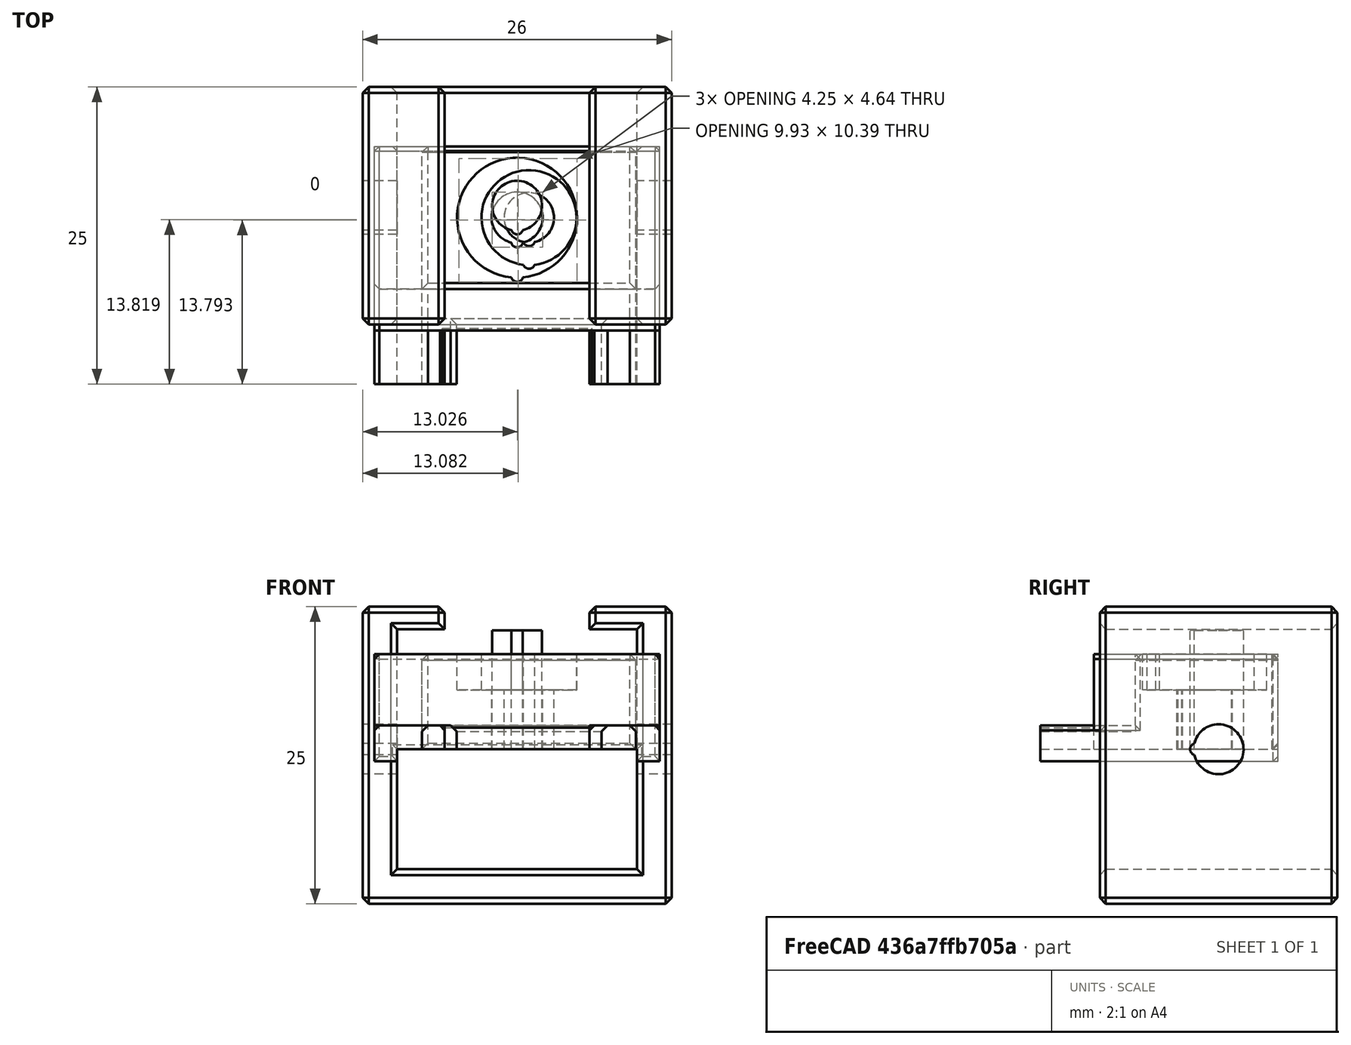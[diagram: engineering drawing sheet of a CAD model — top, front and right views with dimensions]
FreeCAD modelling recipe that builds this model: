
FCSTD DOCUMENT  (FreeCAD 0.18R14555 (Git shallow))
Label: 2020-rail-mount
License: All rights reserved
LicenseURL: http://en.wikipedia.org/wiki/All_rights_reserved
objects: Part::Box×9, Part::Cut×7, Part::Cylinder×6, Part::Feature×6, Part::MultiFuse×6, Part::Chamfer×5
note: 39 computed .brp shape members not serialized (recipe doc carries the construction recipe); baked Part::Feature solids carry a one-line shape summary decoded from their .brp

FEATURE [Part::Box] Box  label="Cube"
  AttacherType = Attacher::AttachEngine3D
  Height = 8
  Length = 24
  Placement = pos=(-12,3,0) rot=(0,0,1;0rad)
  Width = 12
FEATURE [Part::Box] Box001  label="ref"
  AttacherType = Attacher::AttachEngine3D
  Height = 2
  Length = 12.2
  Placement = pos=(-6.1,-5,0) rot=(0,0,1;0rad)
  Width = 4.5
FEATURE [Part::Cylinder] Cylinder
  Angle = 360
  AttacherType = Attacher::AttachEngine3D
  Height = 8
  Placement = pos=(0,7,0) rot=(0,0,1;0rad)
  Radius = 0.5
FEATURE [Part::Feature] Cut001001  label="Cut002"
  shape: bbox 18 x 20 x 8 mm, 17 faces (baked)
FEATURE [Part::Chamfer] Chamfer  label="head-tail"
  Base = -> Cut001001
  Edges = 12 edges r=0.5: [Edge1,Edge3,Edge5,Edge6,Edge7,Edge13,Edge15,Edge16,Edge17,Edge33,Edge34,Edge35]
FEATURE [Part::Box] Box003  label="Cube003"
  AttacherType = Attacher::AttachEngine3D
  Height = 20.2
  Length = 20.2
  Placement = pos=(-10.1,0,-10.1) rot=(0,0,1;0rad)
  Width = 20
FEATURE [Part::Box] Box004  label="Cube004"
  AttacherType = Attacher::AttachEngine3D
  Height = 25
  Length = 26
  Placement = pos=(-13,0,-13) rot=(0,0,1;0rad)
  Width = 20
FEATURE [Part::Box] Box005  label="Cube005"
  AttacherType = Attacher::AttachEngine3D
  Height = 13
  Length = 12.2
  Placement = pos=(-6.1,0,0) rot=(0,0,1;0rad)
  Width = 20
FEATURE [Part::MultiFuse] Fusion002
  Shapes = -> [Box003,Box005]
FEATURE [Part::Cylinder] Cylinder004
  Angle = 360
  AttacherType = Attacher::AttachEngine3D
  Height = 10
  Placement = pos=(0,10,0) rot=(0,0,1;0rad)
  Radius = 2.1
FEATURE [Part::Cylinder] Cylinder005
  Angle = 360
  AttacherType = Attacher::AttachEngine3D
  Height = 10
  Placement = pos=(0,8.1,0) rot=(0,0,1;0rad)
  Radius = 0.5
FEATURE [Part::MultiFuse] Fusion003
  Shapes = -> [Cylinder005,Cylinder004]
FEATURE [Part::Feature] Fusion003001  label="Fusion004"
  Placement = pos=(-6.7,0,-1e-15) rot=(0,-1,0;1.5708rad)
  shape: bbox 10 x 4.5 x 4.2 mm, 9 faces (baked)
FEATURE [Part::Feature] Fusion003002  label="Fusion005"
  Placement = pos=(14.7,0,-5.8e-15) rot=(0,-1,0;1.5708rad)
  shape: bbox 10 x 4.5 x 4.2 mm, 9 faces (baked)
FEATURE [Part::Cut] Cut001002
  Base = -> Box004
  Tool = -> Fusion002
FEATURE [Part::Cut] Cut001003
  Base = -> Cut001002
  Tool = -> Fusion003001
FEATURE [Part::Cut] Cut001004
  Base = -> Cut001003
  Tool = -> Fusion003002
FEATURE [Part::Chamfer] Chamfer002
  Base = -> Cut001004
  Edges = 30 edges r=0.5: [Edge1,Edge2,Edge3,Edge4,Edge8,Edge9,Edge10,Edge11,Edge12,Edge13,Edge14,Edge15,Edge16,Edge17,Edge18,Edge19,Edge20,Edge21,Edge22,Edge23,Edge24,Edge25,Edge26,Edge27,Edge28,Edge29,Edge30,Edge31,Edge38,Edge42]
FEATURE [Part::Cylinder] Cylinder006
  Angle = 360
  AttacherType = Attacher::AttachEngine3D
  Height = 3
  Placement = pos=(0,4.1,5) rot=(0,0,1;0rad)
  Radius = 0.5
FEATURE [Part::Box] Box002  label="Cube002"
  AttacherType = Attacher::AttachEngine3D
  Height = 2
  Length = 24
  Placement = pos=(-12,-5,0) rot=(0,0,1;0rad)
  Width = 20
FEATURE [Part::Cut] Cut
  Base = -> Box002
  Tool = -> Box001
FEATURE [Part::MultiFuse] Fusion
  Shapes = -> [Cut,Box]
FEATURE [Part::Box] Box006  label="Cube006"
  AttacherType = Attacher::AttachEngine3D
  Height = 1
  Length = 1.9
  Placement = pos=(-12,-5,-1) rot=(0,0,1;0rad)
  Width = 20
FEATURE [Part::Box] Box007  label="Cube007"
  AttacherType = Attacher::AttachEngine3D
  Height = 1
  Length = 1.9
  Placement = pos=(10.1,-5,-1) rot=(0,0,1;0rad)
  Width = 20
FEATURE [Part::MultiFuse] Fusion003003
  Shapes = -> [Fusion,Box006,Box007]
FEATURE [Part::Cylinder] Cylinder007
  Angle = 360
  AttacherType = Attacher::AttachEngine3D
  Height = 8
  Placement = pos=(0,9,0) rot=(0,0,1;0rad)
  Radius = 2.15
FEATURE [Part::Cylinder] Cylinder008
  Angle = 360
  AttacherType = Attacher::AttachEngine3D
  Height = 3
  Placement = pos=(0,9,5) rot=(0,0,1;0rad)
  Radius = 5.05
FEATURE [Part::MultiFuse] Fusion003004
  Shapes = -> [Cylinder007,Cylinder008]
FEATURE [Part::Cut] Cut001005
  Base = -> Fusion003003
  Tool = -> Fusion003004
FEATURE [Part::Cut] Cut001006
  Base = -> Cut001005
  Tool = -> Cylinder006
FEATURE [Part::Cut] Cut001007  label="head-align-r1"
  Base = -> Cut001006
  Tool = -> Cylinder
FEATURE [Part::Feature] Cut001007001  label="head-align-r002"
  shape: bbox 24 x 20 x 9 mm, 21 faces (baked)
FEATURE [Part::Chamfer] Chamfer003
  Base = -> Cut001007001
  Edges = 14 edges r=0.4: [Edge3,Edge5,Edge12,Edge17,Edge25,Edge27,Edge28,Edge29,Edge30,Edge38,Edge40,Edge45,Edge47,Edge48]
FEATURE [Part::Chamfer] Chamfer004  label="tail"
  Base = -> Chamfer003
  Edges = 3 edges r=0.2: [Edge30,Edge37,Edge39]
FEATURE [Part::Feature] Cut001007002  label="head-align-r003"
  shape: bbox 24 x 20 x 9 mm, 37 faces (baked)
FEATURE [Part::Box] Box008  label="Cube008"
  AttacherType = Attacher::AttachEngine3D
  Height = 8
  Length = 24
  Placement = pos=(-12,-0.5,0) rot=(0,0,1;0rad)
  Width = 3.5
FEATURE [Part::MultiFuse] Fusion003005
  Shapes = -> [Box008,Cut001007002]
FEATURE [Part::Feature] Fusion003005001  label="Fusion003006"
  shape: bbox 24 x 20 x 9 mm, 21 faces (baked)
FEATURE [Part::Chamfer] Chamfer005  label="big-head"
  Base = -> Fusion003005001
  Edges = 14 edges r=0.4: [Edge3,Edge5,Edge12,Edge14,Edge23,Edge25,Edge28,Edge29,Edge32,Edge37,Edge39,Edge40,Edge47,Edge48]
